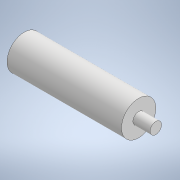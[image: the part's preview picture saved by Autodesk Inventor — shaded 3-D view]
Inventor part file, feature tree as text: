
AUTODESK INVENTOR PART (.ipt)
format: ipt  version: 2022.3 (Build 263350000, 350)  size: 101,376 bytes
history: native  units: mm
features: extrude x2, sketch x2
ambient origin geometry x8: Origin, YZ Plane, XZ Plane, XY Plane, X Axis, Y Axis, Z Axis, Center Point
bodies: Solid1 (feature_tree)
feature tree (4):
  extrude  "Extrusion1"  Depth=20.0mm TaperAngle=0.0deg
  extrude  "Extrusion2"  Depth=3.0mm TaperAngle=0.0deg
  sketch  "Sketch1"  dims[d0=6.0mm d1=20.0mm d2=0.0mm]
  sketch  "Sketch2"  dims[d3=2.0mm d4=3.0mm d5=0.0mm]
